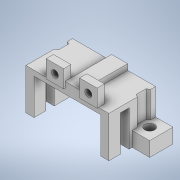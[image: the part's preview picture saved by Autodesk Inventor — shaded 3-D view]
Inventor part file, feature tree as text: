
AUTODESK INVENTOR PART (.ipt)
format: ipt  version: 2022 (Build 260153000, 153)  size: 235,008 bytes
history: native  units: mm
features: extrude x5, sketch x4, other x1
ambient origin geometry x8: Origin, YZ Plane, XZ Plane, XY Plane, X Axis, Y Axis, Z Axis, Center Point
bodies: Body1 (feature_tree)
feature tree (10):
  other  "FS90R.ipt"
  sketch  "スケッチ2"
  extrude  "ベース"  Depth=10.0mm
  extrude  "タブ切欠き"  Depth=12.1mm
  extrude  "マウント"  Depth=22.5mm
  extrude  "基板マウントタブ"  Depth=0.2mm
  extrude  "ナット逃げ"  Depth=0.2mm
  sketch  "スケッチ3"
  sketch  "スケッチ4"
  sketch  "スケッチ5"
